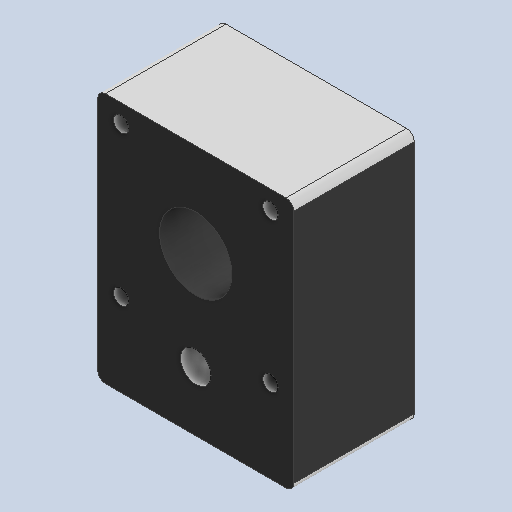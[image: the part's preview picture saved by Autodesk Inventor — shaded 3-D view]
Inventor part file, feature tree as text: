
AUTODESK INVENTOR PART (.ipt)
format: ipt  version: 2025.1 (Build 291241020, 241B)  size: 149,504 bytes
history: native  units: in
note: dims shown in document units (in); Inventor stores cm internally (conversion verified against a paired STEP export)
features: extrude x3, sketch x3, fillet x1
ambient origin geometry x8: Origin, YZ Plane, XZ Plane, XY Plane, X Axis, Y Axis, Z Axis, Center Point
bodies: Solid1 (feature_tree)
feature tree (7):
  extrude  "Extrusion1"  Depth=1.6in
  extrude  "Extrusion2"  Depth=0.9843in
  extrude  "Extrusion3"  Depth=0.063in TaperAngle=0.0deg
  fillet  "Fillet1"  Radius=0.25in
  sketch  "Sketch1"  dims[d0=1.6in d1=2.1in]
  sketch  "Sketch2"  dims[d2=0.9843in d3=0.0in d4=0.8125in]
  sketch  "Sketch3"  dims[d5=0.5906in d6=0.5in d7=0.0in d8=0.25in d9=0.8in d11=0.125in d12=0.6102in d13=0.6102in d14=0.05in d15=0.0in d16=0.063in]
